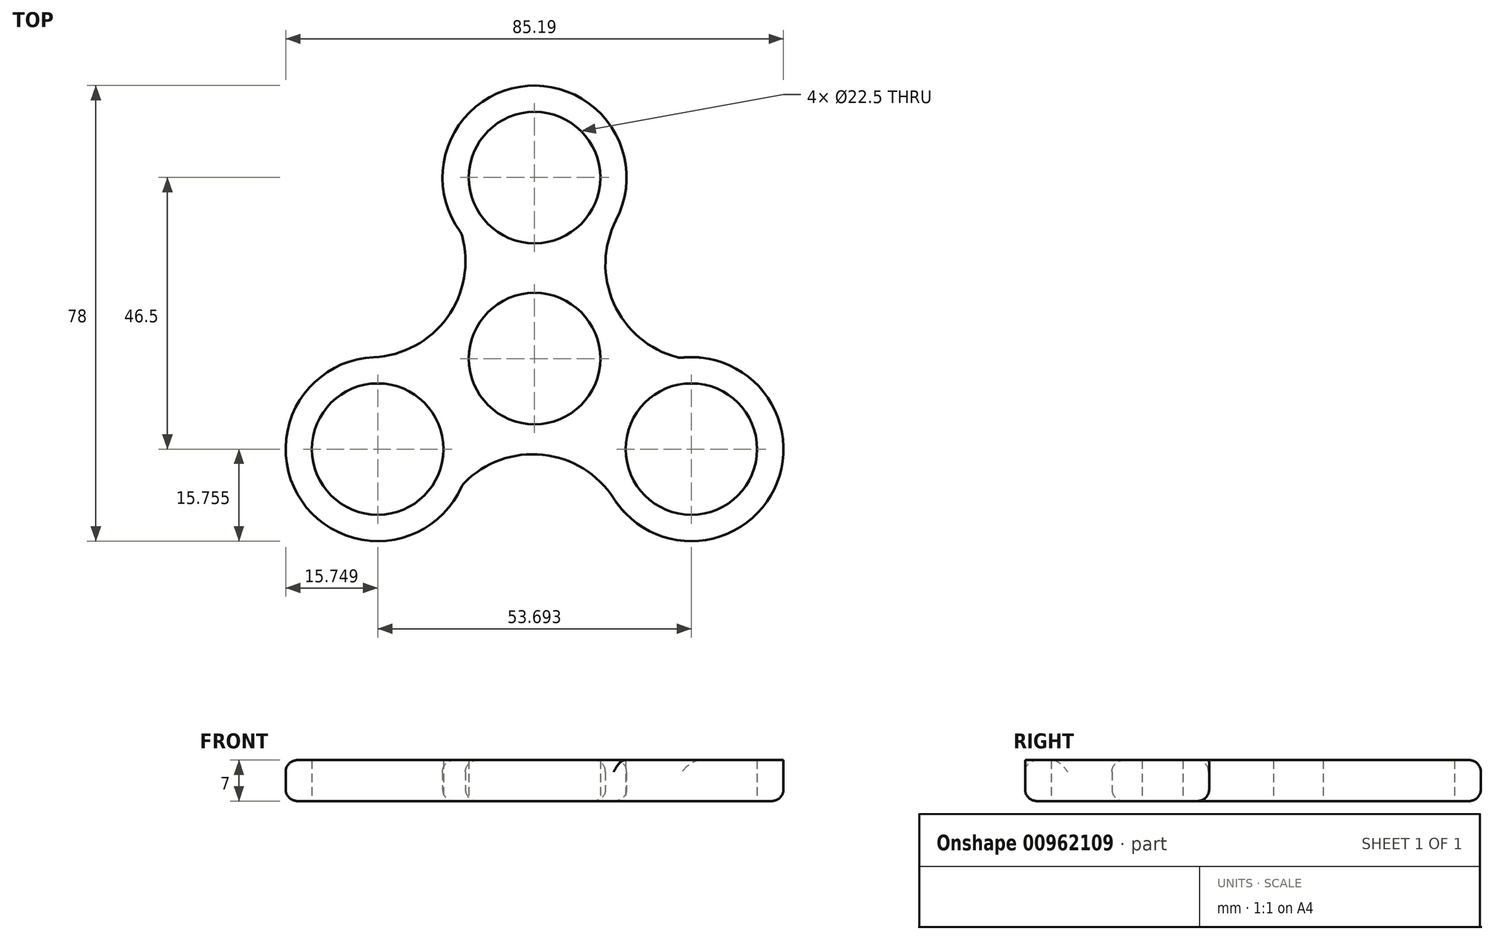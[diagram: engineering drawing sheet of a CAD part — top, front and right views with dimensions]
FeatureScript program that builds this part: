
annotation { "Feature Type Name" : "Feature", "Feature Type Description" : "" }
export const myFeature = defineFeature(function(context is Context, id is Id, definition is map)
    precondition{}
    {
        {
            var Q0;
            Q0=qCreatedBy(makeId("Top.planeOp"),FACE);
            var sketch = newSketch(context, id + "F0", { "sketchPlane" : qUnion([Q0])});
            skCircle(sketch, "E0", {"center": v(-71.38, 7.53) * mm, "radius": 11.25 * mm});
            skCircle(sketch, "E1", {"center": v(-71.38, -23.47) * mm, "radius": 11.25 * mm});
            skCircle(sketch, "E2.1.0", {"center": v(-98.23, -38.97) * mm, "radius": 11.25 * mm});
            skCircle(sketch, "E2.2.0", {"center": v(-44.54, -38.97) * mm, "radius": 11.25 * mm});
            skCircle(sketch, "E3.0", {"center": v(-71.38, 7.53) * mm, "radius": 15.75 * mm});
            skCircle(sketch, "E4.0", {"center": v(-44.54, -38.97) * mm, "radius": 15.75 * mm});
            skCircle(sketch, "E5.0", {"center": v(-98.23, -38.97) * mm, "radius": 15.75 * mm});
            skArc(sketch, "E6", {"start": v(-98.91, -23.23) * mm, "mid": v(-86.23, -16.28) * mm, "end": v(-83.92, -2) * mm});
            skArc(sketch, "E7.1.0", {"start": v(-57.82, -47.42) * mm, "mid": v(-70.18, -39.91) * mm, "end": v(-83.7, -45.05) * mm});
            skArc(sketch, "E7.2.0", {"start": v(-57.42, 0.26) * mm, "mid": v(-57.74, -14.2) * mm, "end": v(-46.53, -23.34) * mm});
            skSolve(sketch);
        }
        {
            var Q0;
            Q0=makeQuery(id+"F0.imprint","IMPRINT",FACE,{"disambiguationData":[TD([[makeQuery(id+"F0.imprint","IMPRINT",EDGE,{"derivedFrom":sQuery(id+"F0.wireOp",EDGE,"E1")}),-1.0]])]});
            var Q1;
            Q1=makeQuery(id+"F0.imprint","IMPRINT",FACE,{"disambiguationData":[TD([[makeQuery(id+"F0.imprint","IMPRINT",EDGE,{"derivedFrom":sQuery(id+"F0.wireOp",EDGE,"E2.2.0")}),-1.0]])]});
            var Q2;
            Q2=makeQuery(id+"F0.imprint","IMPRINT",FACE,{"disambiguationData":[TD([[makeQuery(id+"F0.imprint","IMPRINT",EDGE,{"derivedFrom":sQuery(id+"F0.wireOp",EDGE,"E2.1.0")}),-1.0]])]});
            var Q3;
            Q3=makeQuery(id+"F0.imprint","IMPRINT",FACE,{"disambiguationData":[TD([[makeQuery(id+"F0.imprint","IMPRINT",EDGE,{"derivedFrom":sQuery(id+"F0.wireOp",EDGE,"E0")}),-1.0]])]});
            extrude(context, id + "F1", {"entities" : qUnion([Q0, Q1, Q2, Q3]), "depth" : 7 * mm, "offsetDistance" : 25 * mm});
        }
        {
            var Q0;
            Q0=makeQuery(id+"F1.opExtrude","SWEPT_FACE",FACE,{"disambiguationData":[OSD([sQuery(id+"F0.wireOp",EDGE,"E3.0")])]});
            var Q1;
            Q1=makeQuery(id+"F1.opExtrude","SWEPT_FACE",FACE,{"disambiguationData":[OSD([sQuery(id+"F0.wireOp",EDGE,"E7.2.0")])]});
            var Q2;
            Q2=makeQuery(id+"F1.opExtrude","CAP_EDGE",EDGE,{"disambiguationData":[OSD([sQuery(id+"F0.wireOp",EDGE,"E4.0")])],"isStart":true});
            var Q3;
            Q3=makeQuery(id+"F1.opExtrude","SWEPT_FACE",FACE,{"disambiguationData":[OSD([sQuery(id+"F0.wireOp",EDGE,"E7.1.0")])]});
            var Q4;
            Q4=makeQuery(id+"F1.opExtrude","SWEPT_FACE",FACE,{"disambiguationData":[OSD([sQuery(id+"F0.wireOp",EDGE,"E5.0")])]});
            var Q5;
            Q5=makeQuery(id+"F1.opExtrude","SWEPT_FACE",FACE,{"disambiguationData":[OSD([sQuery(id+"F0.wireOp",EDGE,"E6")])]});
            fillet(context, id + "F2", {"entities" : qUnion([Q0, Q1, Q2, Q3, Q4, Q5]), "radius" : 2 * mm, "tangentPropagation" : true, "allowEdgeOverflow" : false});
        }
    });
